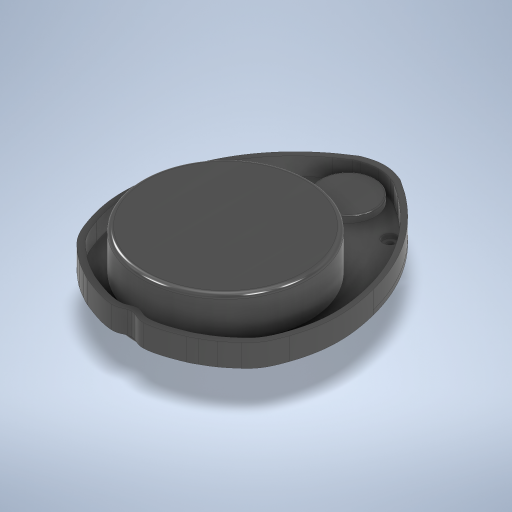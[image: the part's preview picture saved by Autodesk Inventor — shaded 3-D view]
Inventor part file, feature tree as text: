
AUTODESK INVENTOR PART (.ipt)
format: ipt  version: 2023.2 (Build 272271000, 271)  size: 555,008 bytes
history: native  units: mm
features: extrude x11, sketch x4, fillet x3, other x1
ambient origin geometry x8: Origin, YZ Plane, XZ Plane, XY Plane, X Axis, Y Axis, Z Axis, Center Point
bodies: Body1 (feature_tree)
feature tree (19):
  other  "Sólido1"
  sketch  "Esboço1"  dims[d0=8.0mm d1=0.0mm d5=24.0mm]
  extrude  "Extrusão1"  Depth=24.0mm
  extrude  "Extrusão3"  Depth=3.5mm
  extrude  "Extrusão4"  Depth=20.0mm TaperAngle=0.0deg
  extrude  "Extrusão5"  Depth=2.0mm TaperAngle=0.0deg
  extrude  "Extrusão6"  Depth=2.0mm TaperAngle=0.0deg
  extrude  "Extrusão7"  Depth=2.0mm TaperAngle=0.0deg
  extrude  "Extrusão8"  Depth=2.0mm TaperAngle=0.0deg
  extrude  "Extrusão9"  Depth=2.0mm TaperAngle=0.0deg
  fillet  "Arredondamento1"  Radius=2.0mm
  fillet  "Arredondamento2"  Radius=1.0mm
  extrude  "Extrusão10"  Depth=0.5mm
  extrude  "Extrusão11"  Depth=0.5mm
  fillet  "Arredondamento3"  Radius=15.0mm
  extrude  "Extrusão12"  Depth=0.5mm
  sketch  "Esboço4"  dims[d6=3.5mm d7=75.0mm]
  sketch  "Esboço5"  dims[d8=55.0mm d9=20.0mm d10=0.0mm]
  sketch  "Esboço6"  dims[d11=5.0mm d12=0.0mm d13=2.0mm d14=0.0mm d15=2.0mm d16=0.0mm d17=2.0mm d18=0.0mm d19=2.0mm d20=0.0mm d21=2.0mm d22=0.0mm d23=2.0mm d24=1.0mm d47=0.5mm d48=32.5mm d49=15.0mm d50=0.0mm d51=80.0mm d52=4.0mm d53=0.0mm d54=1.5mm d55=3.0mm d56=3.0mm d57=6.0mm d58=0.0mm d60=8.0mm d61=8.0mm d59=0.5mm]
